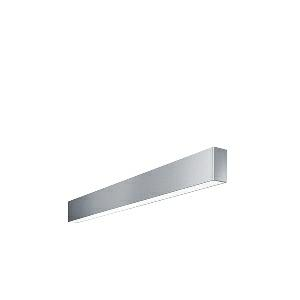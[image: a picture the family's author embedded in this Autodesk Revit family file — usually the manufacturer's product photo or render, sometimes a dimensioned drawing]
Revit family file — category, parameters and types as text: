
# Revit family: idoo_line_-_ilw_2000_830_d_00808327_83b7
name_source: partatom
category: Lighting Fixtures
units: mm (PartAtom-declared; Revit-internal decimal feet)

## family parameters
Cut with Voids When Loaded = No
Host = Face
Light Source = No
Part Type = Normal
Room Calculation Point = No
Round Connector Dimension = Use Diameter
Shared = No

## types (1)
- IDOO.line - ILW 2000/830/D (1 x LED, 2250 lm, 3000K)
    Apparent Load = 17 VA
    Approval mark = CE
    CIE Flux Codes = 66 91 98 40 100
    Color Rendering = 80-89
    Color Temperature = 3000K
    Control Gear = Electronic ballast
    Default Elevation = 2000 mm  [stored 6.56168 ft]
    Description = ILW 2000/830/D|Wall-mounted luminaire|light source:  |work equipment: Adjustable electronic ballast, digital DALI|connected load: 220-240V, 50/60Hz|Power consumption: approx. 17 W|standby: approx. 0,25|power factor: approx. 0,970|luminous flux: 2250 lm|luminous efficacy: 132 lm/W|light distribution: Direct/indirect|direct ratio: approx. 40 %|colour temperature: Warm white, ca. 3000 K|color rendering index (CRI): >= 80|chromaticity tolerance:  3 SDCM|technology: Continuously dimmable|operation: External|luminaire body|material: Sectional aluminium|colour: Silver|lamp cover: Acrylic (PMMA), Clear|weight (net): approx. 3.9 kg|mains lead: Connector|design: Mounted version|Fastening: Mounting rail|glare control: Prism aperture|luminance(L65): <= 2700 cd/m|unified glare rating(4H 8H): <=  16|special features: DALI Load 1x, TouchDIM - dimming via standard switch, Flicker-free, Suitable as emergency lighting|
    Frequency = 50 Hz
    Height = 110 mm
    Lamp = 1 x LED
    Lamp Light Flux = 2250 lm
    Lamp count = 1
    Length = 854 mm
    Luminous efficacy = 132 lm/W
    Manufacturer = Waldmann
    ModVariant = No
    Model = 00808327
    Mounting Place = Wall
    Mounting Type = Surface mounted
    Number of Poles = 1
    OnlyDefault = Yes
    Power Factor = 1
    Product Name = IDOO.line - ILW 2000/830/D
    Product group = Wall mounted Luminaire
    ProductGroupID = 20
    Protection Class = Protection class I
    Protection Degree = IP 40
    RLX_Detail_Level = 1
    RLX_Emergency_Light_Flux = 0 lm
    RLX_Emergency_Type = 0
    RLX_Emergency_Type_DB = No
    RlxData = <blob elided: 33433 chars, md5=1014ae70>
    Socket = socket
    Standby Power = 0 W
    System Light Flux = 2250 lm
    System Power = 17 W
    Type Comments = Product without accessories
    Type Image = 113974000-00757978.jpg
    URL = http://relux.com
    VarID = ---
    Voltage = 230 V
    Voltage Range = 220-240 V
    Weight = 0.00 kg
    Width = 60 mm  [stored 0.19685 ft]

note: [stored X ft] marks values corroborated as IEEE doubles in the binary element streams (Revit-internal decimal feet)

## geometry (parser evidence)
native form markers: Blend x4, Sweep x13
no freeform markers — native parametric forms only
